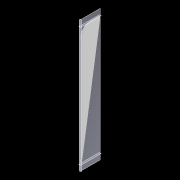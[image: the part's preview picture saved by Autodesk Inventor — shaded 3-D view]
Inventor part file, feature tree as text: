
AUTODESK INVENTOR PART (.ipt)
format: ipt  version: 2020 (Build 240168000, 168)  size: 90,112 bytes
history: native  units: mm
features: other x1, extrude x1, plane x1, fillet x1, sketch x1
ambient origin geometry x8: Origin, YZ Plane, XZ Plane, XY Plane, X Axis, Y Axis, Z Axis, Center Point
bodies: Body1 (feature_tree)
feature tree (5):
  other  "實體1"
  extrude  "擠出1"  Depth=106.071mm
  plane  "工作平面1"
  fillet  "圓角1"  Radius=674.096mm
  sketch  "草圖1"
